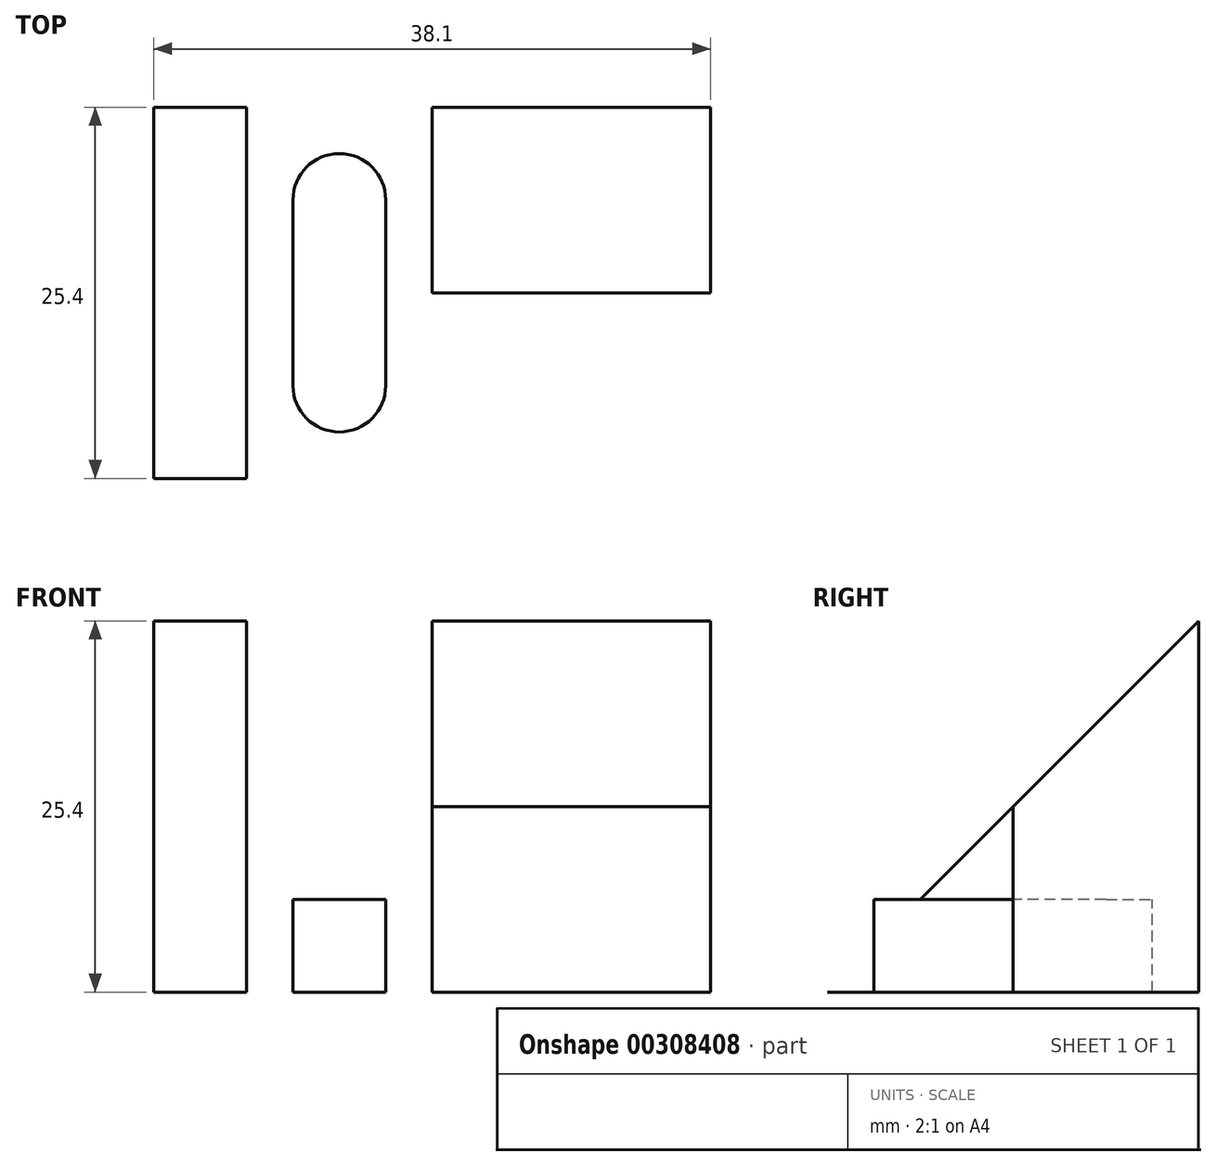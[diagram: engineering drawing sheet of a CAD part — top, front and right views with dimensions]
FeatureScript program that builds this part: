
annotation { "Feature Type Name" : "Feature", "Feature Type Description" : "" }
export const myFeature = defineFeature(function(context is Context, id is Id, definition is map)
    precondition{}
    {
        {
            var Q0;
            Q0=qCreatedBy(makeId("Front.planeOp"),FACE);
            var sketch = newSketch(context, id + "F0", { "sketchPlane" : qUnion([Q0])});
            skLineSegment(sketch, "E0", {"start": v(0, 0) * mm, "end": v(0, 25.4) * mm});
            skLineSegment(sketch, "E1", {"start": v(0, 25.4) * mm, "end": v(6.35, 25.4) * mm});
            skLineSegment(sketch, "E2", {"start": v(6.35, 25.4) * mm, "end": v(6.35, 0) * mm});
            skLineSegment(sketch, "E3", {"start": v(6.35, 0) * mm, "end": v(0, 0) * mm});
            skLineSegment(sketch, "E4", {"start": v(6.35, 0) * mm, "end": v(38.1, 0) * mm});
            skLineSegment(sketch, "E5", {"start": v(38.1, 0) * mm, "end": v(38.1, 25.4) * mm});
            skLineSegment(sketch, "E6", {"start": v(38.1, 25.4) * mm, "end": v(19.05, 25.4) * mm});
            skLineSegment(sketch, "E7", {"start": v(19.05, 25.4) * mm, "end": v(19.05, 0) * mm});
            skLineSegment(sketch, "E8", {"start": v(19.05, 12.7) * mm, "end": v(38.1, 12.7) * mm});
            skLineSegment(sketch, "E9", {"start": v(6.35, 6.35) * mm, "end": v(19.05, 6.35) * mm});
            skSolve(sketch);
        }
        {
            var Q0;
            {var subQ3=sQuery(id+"F0.wireOp",EDGE,"E9");Q0=makeQuery(id+"F0.imprint","IMPRINT",FACE,{"disambiguationData":[TD([[makeQuery(id+"F0.imprint","IMPRINT",EDGE,{"derivedFrom":subQ3}),-1.0]])]});}
            extrude(context, id + "F1", {"entities" : qUnion([Q0]), "depth" : 25.4 * mm, "symmetric" : true});
        }
        {
            var Q0;
            Q0=makeQuery(id+"F1.opExtrude","SWEPT_FACE",FACE,{"disambiguationData":[OSD([sQuery(id+"F0.wireOp",EDGE,"E9")])]});
            var sketch = newSketch(context, id + "F2", { "sketchPlane" : qUnion([Q0])});
            skLineSegment(sketch, "E10", {"start": v(12.7, 6.35) * mm, "end": v(12.7, -6.35) * mm, "construction": true});
            skPoint(sketch, "E10.startSnap0", {"position": v(12.7, 12.7) * mm});
            skArc(sketch, "E11.0.startCap", {"start": v(9.53, 6.35) * mm, "mid": v(12.7, 9.52) * mm, "end": v(15.88, 6.35) * mm});
            skArc(sketch, "E11.0.endCap", {"start": v(15.88, -6.35) * mm, "mid": v(12.7, -9.53) * mm, "end": v(9.53, -6.35) * mm});
            skLineSegment(sketch, "E11.0.left", {"start": v(15.88, 6.35) * mm, "end": v(15.88, -6.35) * mm});
            skLineSegment(sketch, "E11.0.right", {"start": v(9.53, 6.35) * mm, "end": v(9.53, -6.35) * mm});
            skSolve(sketch);
        }
        {
            var Q0;
            Q0=makeQuery(id+"F2.imprint","IMPRINT",FACE,{"disambiguationData":[TD([[makeQuery(id+"F2.imprint","IMPRINT",EDGE,{"derivedFrom":sQuery(id+"F2.wireOp",EDGE,"E11.0.startCap")}),-1.0]])]});
            extrude(context, id + "F3", {"entities" : qUnion([Q0]), "operationType" : NewBodyOperationType.REMOVE, "endBound" : BoundingType.THROUGH_ALL, "oppositeDirection" : true, "depth" : 25.4 * mm});
        }
        {
            var Q0;
            {var subQ6=sQuery(id+"F0.wireOp",EDGE,"E8");Q0=makeQuery(id+"F0.imprint","IMPRINT",FACE,{"disambiguationData":[TD([[makeQuery(id+"F0.imprint","IMPRINT",EDGE,{"derivedFrom":subQ6}),-1.0]])]});}
            var Q1;
            {var subQ0=sQuery(id+"F0.wireOp",EDGE,"E6");Q1=makeQuery(id+"F0.imprint","IMPRINT",FACE,{"disambiguationData":[TD([[makeQuery(id+"F0.imprint","IMPRINT",EDGE,{"derivedFrom":subQ0}),1.0]])]});}
            extrude(context, id + "F4", {"entities" : qUnion([Q0, Q1]), "operationType" : NewBodyOperationType.ADD, "depth" : 25.4 * mm, "symmetric" : true});
        }
        {
            var Q0;
            Q0=makeQuery(id+"F4.opExtrude","SWEPT_FACE",FACE,{"disambiguationData":[OSD([sQuery(id+"F0.wireOp",EDGE,"E5")])]});
            var sketch = newSketch(context, id + "F5", { "sketchPlane" : qUnion([Q0])});
            skLineSegment(sketch, "E12", {"start": v(12.7, 25.4) * mm, "end": v(-12.7, 0) * mm});
            skSolve(sketch);
        }
        {
            var Q0;
            Q0=makeQuery(id+"F0.imprint","IMPRINT",FACE,{"disambiguationData":[TD([[makeQuery(id+"F0.imprint","IMPRINT",EDGE,{"derivedFrom":sQuery(id+"F0.wireOp",EDGE,"E0")}),-1.0]])]});
            extrude(context, id + "F6", {"entities" : qUnion([Q0]), "operationType" : NewBodyOperationType.ADD, "depth" : 25.4 * mm, "symmetric" : true});
        }
        {
            var Q0;
            Q0=makeQuery(id+"F5.imprint","IMPRINT",FACE,{"disambiguationData":[TD([[makeQuery(id+"F5.imprint","IMPRINT",EDGE,{"derivedFrom":sQuery(id+"F5.wireOp",EDGE,"E12")}),-1.0]])]});
            extrude(context, id + "F7", {"entities" : qUnion([Q0]), "operationType" : NewBodyOperationType.REMOVE, "oppositeDirection" : true, "depth" : 19.05 * mm});
        }
        {
            var Q0;
            Q0=makeQuery(id+"F4.opExtrude","SWEPT_FACE",FACE,{"disambiguationData":[OSD([sQuery(id+"F0.wireOp",EDGE,"E5")])]});
            var sketch = newSketch(context, id + "F8", { "sketchPlane" : qUnion([Q0])});
            skLineSegment(sketch, "E13", {"start": v(0, 12.7) * mm, "end": v(0, 0) * mm});
            skSolve(sketch);
        }
        {
            var Q0;
            {var subQ0=sQuery(id+"F8.wireOp",EDGE,"E13");Q0=makeQuery(id+"F8.imprint","IMPRINT",FACE,{"disambiguationData":[TD([[makeQuery(id+"F8.imprint","IMPRINT",EDGE,{"derivedFrom":subQ0}),-1.0]])]});}
            extrude(context, id + "F9", {"entities" : qUnion([Q0]), "operationType" : NewBodyOperationType.REMOVE, "oppositeDirection" : true, "depth" : 19.05 * mm});
        }
        {
            var Q0;
            Q0=makeQuery(id+"F6.opExtrude","SWEPT_FACE",FACE,{"disambiguationData":[OSD([sQuery(id+"F0.wireOp",EDGE,"E0")])]});
            var sketch = newSketch(context, id + "F10", { "sketchPlane" : qUnion([Q0])});
            skLineSegment(sketch, "E14", {"start": v(-12.7, 25.4) * mm, "end": v(12.7, 0) * mm});
            skSolve(sketch);
        }
        {
            var Q0;
            Q0=makeQuery(id+"F10.imprint","IMPRINT",FACE,{"disambiguationData":[TD([[makeQuery(id+"F10.imprint","IMPRINT",EDGE,{"derivedFrom":sQuery(id+"F10.wireOp",EDGE,"E14")}),1.0]])]});
            extrude(context, id + "F11", {"entities" : qUnion([Q0]), "operationType" : NewBodyOperationType.REMOVE, "oppositeDirection" : true, "depth" : 6.35 * mm});
        }
    });
